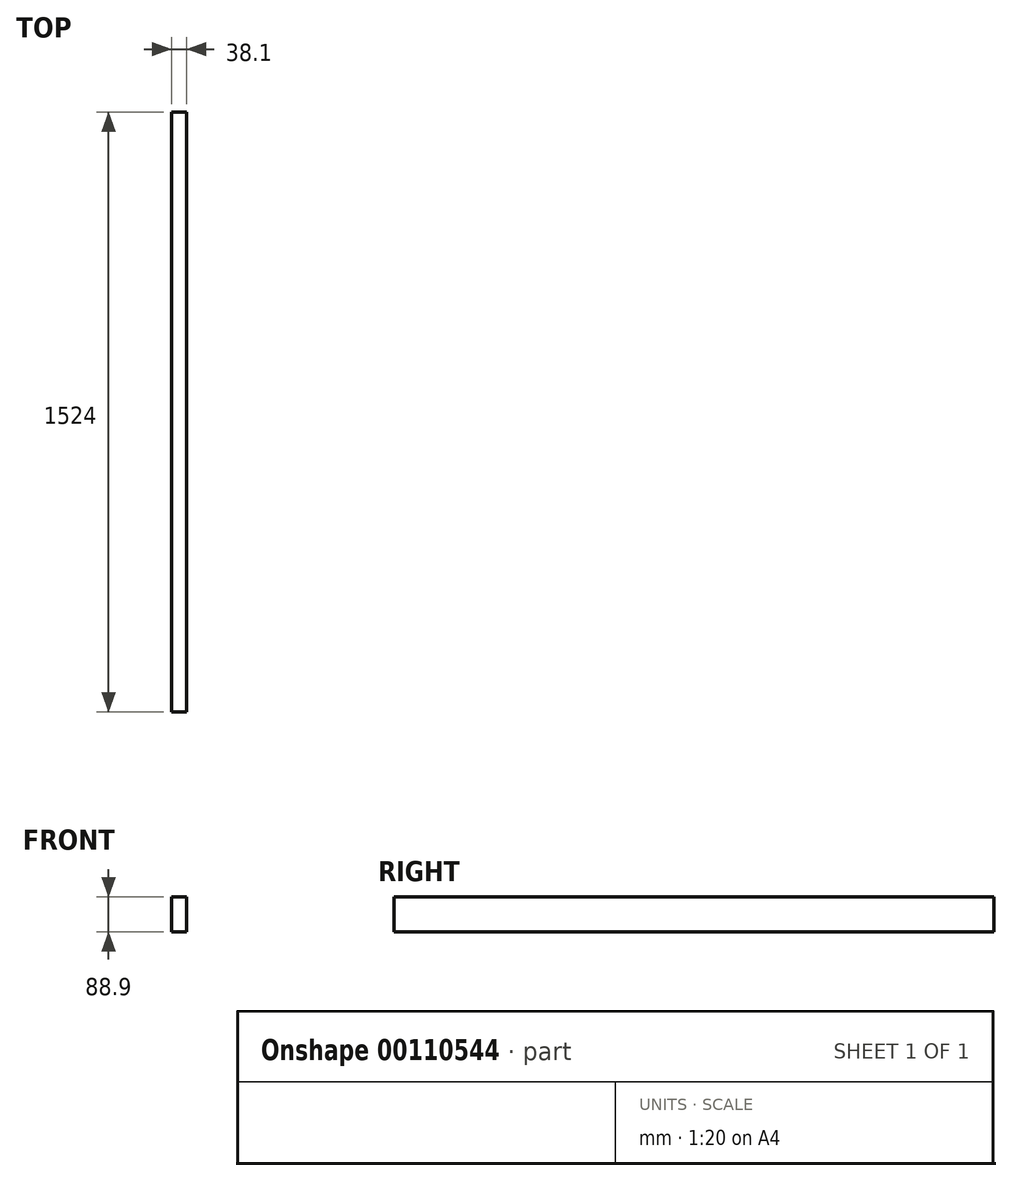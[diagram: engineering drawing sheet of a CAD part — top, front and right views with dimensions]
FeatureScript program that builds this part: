
annotation { "Feature Type Name" : "Feature", "Feature Type Description" : "" }
export const myFeature = defineFeature(function(context is Context, id is Id, definition is map)
    precondition{}
    {
        {
            var Q0;
            Q0=qCreatedBy(makeId("Front.planeOp"),FACE);
            var sketch = newSketch(context, id + "F0", { "sketchPlane" : qUnion([Q0])});
            skLineSegment(sketch, "E0.bottom", {"start": v(19.05, 44.45) * mm, "end": v(-19.05, 44.45) * mm});
            skLineSegment(sketch, "E0.top", {"start": v(19.05, -44.45) * mm, "end": v(-19.05, -44.45) * mm});
            skLineSegment(sketch, "E0.left", {"start": v(19.05, 44.45) * mm, "end": v(19.05, -44.45) * mm});
            skLineSegment(sketch, "E0.right", {"start": v(-19.05, 44.45) * mm, "end": v(-19.05, -44.45) * mm});
            skPoint(sketch, "E0.middle", {"position": v(0, 0) * mm});
            skSolve(sketch);
        }
        {
            var Q0;
            Q0=makeQuery(id+"F0.imprint","IMPRINT",FACE,{"disambiguationData":[TD([[makeQuery(id+"F0.imprint","IMPRINT",EDGE,{"derivedFrom":sQuery(id+"F0.wireOp",EDGE,"E0.bottom")}),1.0]])]});
            extrude(context, id + "F1", {"entities" : qUnion([Q0]), "endBound" : BoundingType.SYMMETRIC, "depth" : 1524 * mm});
        }
    });
